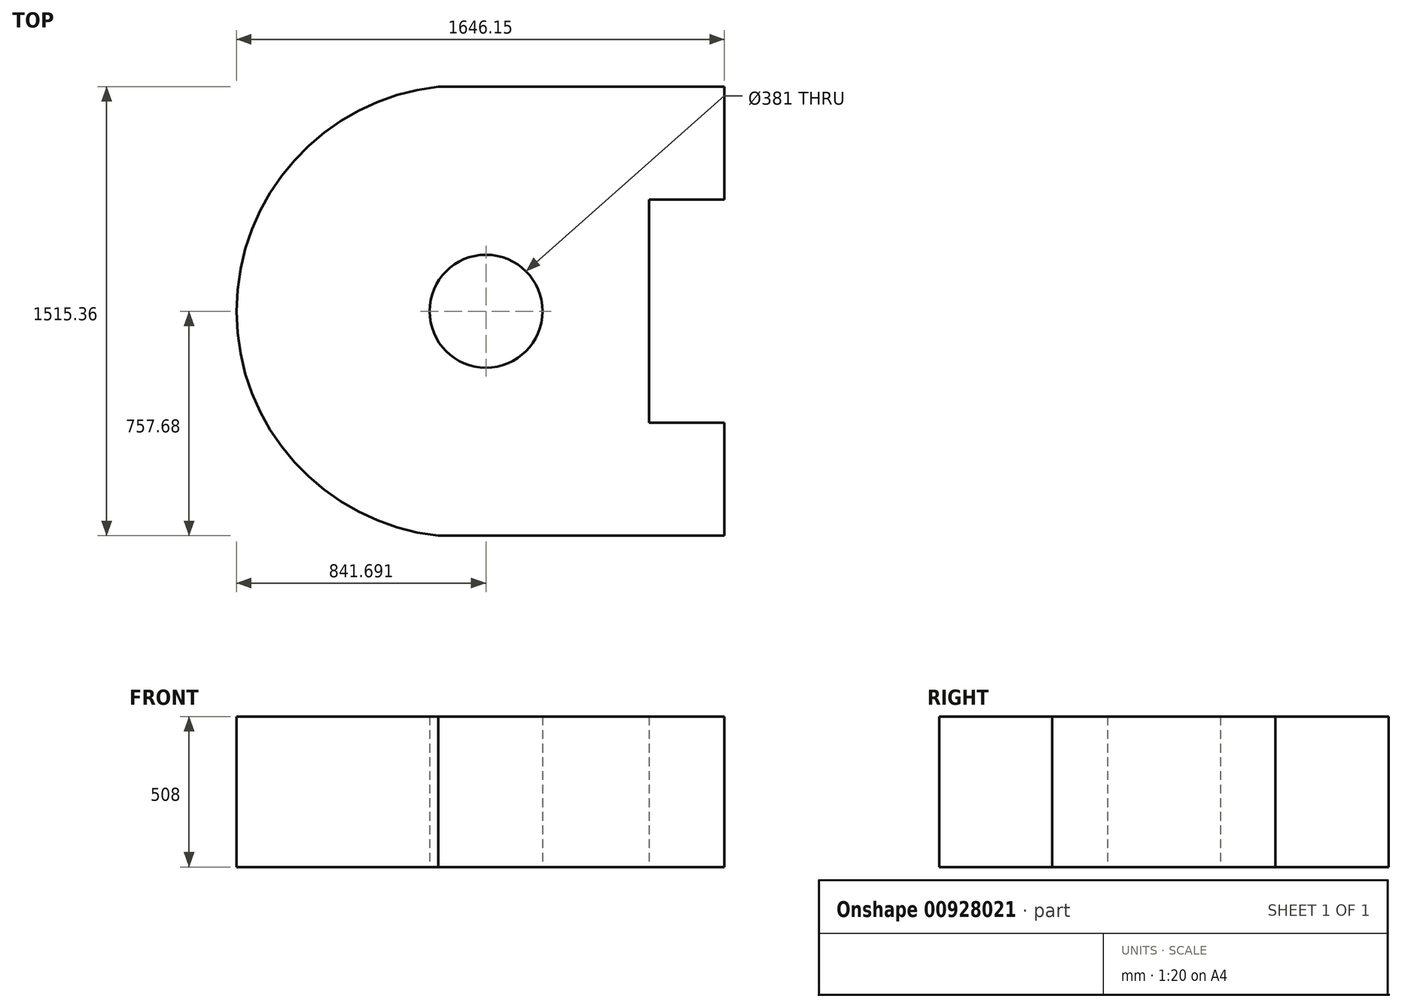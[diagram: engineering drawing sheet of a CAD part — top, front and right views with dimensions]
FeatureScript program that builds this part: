
annotation { "Feature Type Name" : "Feature", "Feature Type Description" : "" }
export const myFeature = defineFeature(function(context is Context, id is Id, definition is map)
    precondition{}
    {
        {
            var Q0;
            Q0=qCreatedBy(makeId("Top.planeOp"),FACE);
            var sketch = newSketch(context, id + "F0", { "sketchPlane" : qUnion([Q0])});
            skLineSegment(sketch, "E0.bottom", {"start": v(-909.52, 857.75) * mm, "end": v(55.68, 857.75) * mm});
            skLineSegment(sketch, "E0.top", {"start": v(-909.52, -657.6) * mm, "end": v(55.68, -657.6) * mm});
            skArc(sketch, "E1", {"start": v(-909.52, 857.75) * mm, "mid": v(-1590.47, 100.07) * mm, "end": v(-909.52, -657.6) * mm});
            skLineSegment(sketch, "E2", {"start": v(55.68, -657.6) * mm, "end": v(55.68, -276.6) * mm});
            skLineSegment(sketch, "E3", {"start": v(55.68, -276.6) * mm, "end": v(-198.32, -276.6) * mm});
            skLineSegment(sketch, "E4", {"start": v(-198.32, -276.6) * mm, "end": v(-198.32, 476.75) * mm});
            skLineSegment(sketch, "E5", {"start": v(-198.32, 476.75) * mm, "end": v(55.68, 476.75) * mm});
            skLineSegment(sketch, "E6", {"start": v(55.68, 476.75) * mm, "end": v(55.68, 857.75) * mm});
            skCircle(sketch, "E7", {"center": v(-748.78, 100.07) * mm, "radius": 190.5 * mm});
            skSolve(sketch);
        }
        {
            var Q0;
            Q0 = qSketchRegion(id + "F0", true);
            extrude(context, id + "F1", {"entities" : qUnion([Q0]), "depth" : 508 * mm, "offsetDistance" : 25.4 * mm});
        }
    });
